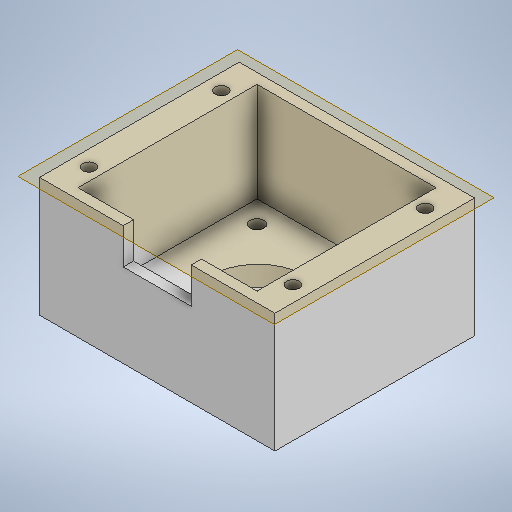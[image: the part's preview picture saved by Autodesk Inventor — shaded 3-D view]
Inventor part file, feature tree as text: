
AUTODESK INVENTOR PART (.ipt)
format: ipt  version: 2025.2 (Build 292293000, 293)  size: 450,048 bytes
history: native  units: mm
features: sketch x6, extrude x3, hole x3, other x2
ambient origin geometry x8: Origin, YZ Plane, XZ Plane, XY Plane, X Axis, Y Axis, Z Axis, Center Point
bodies: Body1 (feature_tree)
feature tree (14):
  other  "ソリッド1"
  extrude  "押し出し1"  Depth=56.0mm
  other  "作業平面2"
  extrude  "押し出し2"  Depth=47.5mm
  hole  "穴1"  [1 undecoded]
  hole  "穴2"  [1 undecoded]
  hole  "穴3"  [1 undecoded]
  extrude  "押し出し3"  Depth=41.5mm
  sketch  "スケッチ1"
  sketch  "スケッチ3"
  sketch  "スケッチ4"
  sketch  "スケッチ5"
  sketch  "スケッチ6"
  sketch  "スケッチ7"
note: 3 required parameter values undecoded (feature->parameter linkage not recoverable at this tier; creation-order binding heuristic only, values carry confidence <= 0.55)
